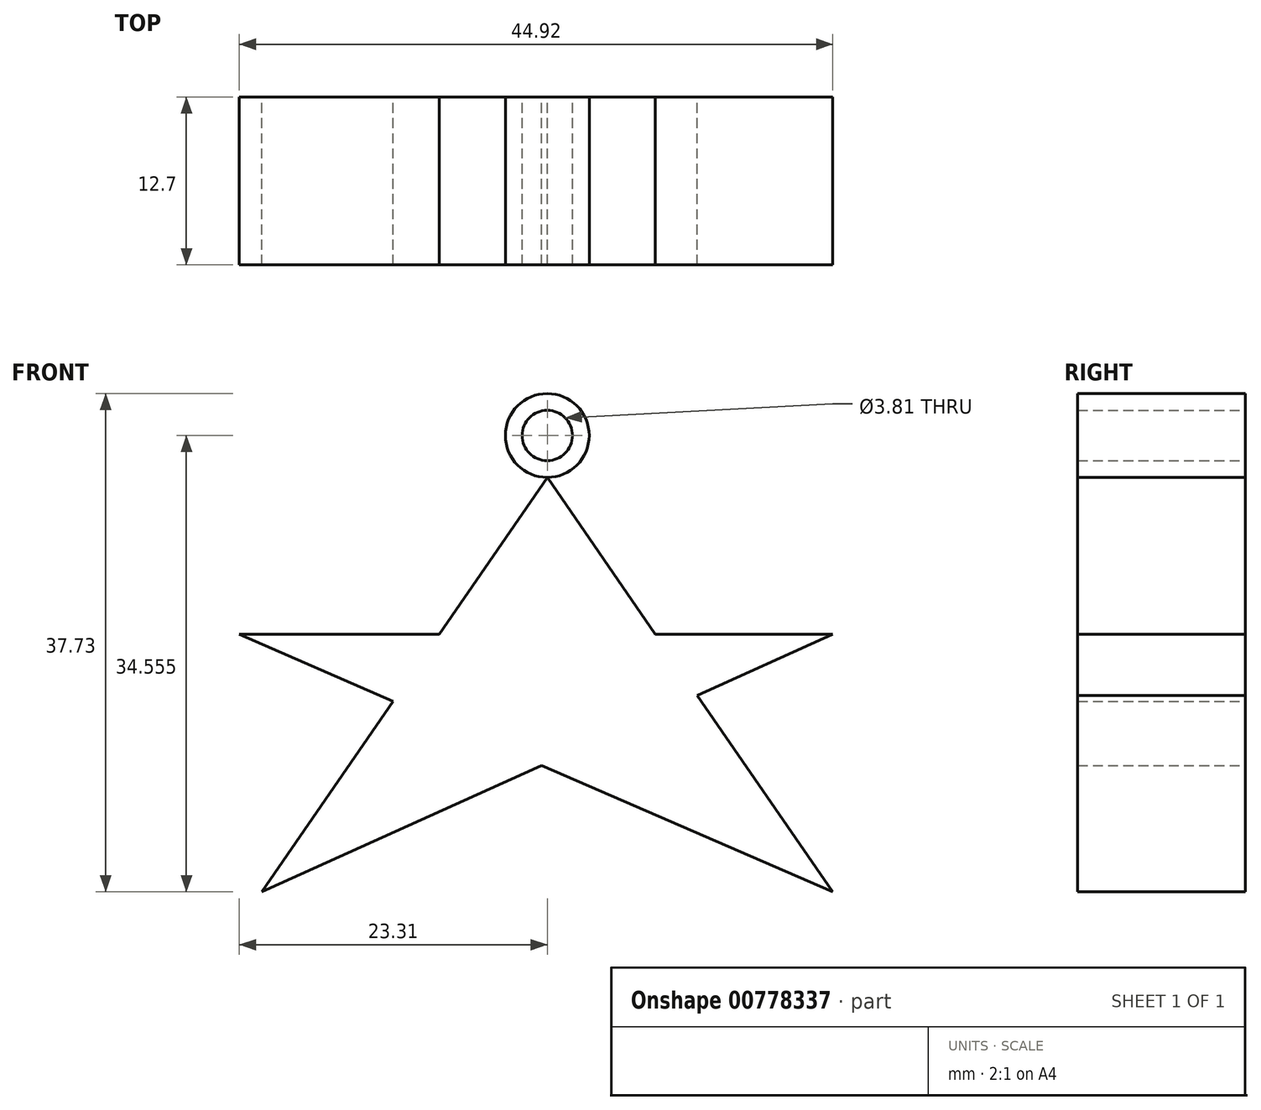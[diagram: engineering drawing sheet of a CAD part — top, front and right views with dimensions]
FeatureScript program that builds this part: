
annotation { "Feature Type Name" : "Feature", "Feature Type Description" : "" }
export const myFeature = defineFeature(function(context is Context, id is Id, definition is map)
    precondition{}
    {
        {
            var Q0;
            Q0=qCreatedBy(makeId("Front.planeOp"),FACE);
            var sketch = newSketch(context, id + "F0", { "sketchPlane" : qUnion([Q0])});
            skLineSegment(sketch, "E0", {"start": v(0, 0) * mm, "end": v(-21.6, -31.38) * mm});
            skLineSegment(sketch, "E1", {"start": v(0, 0) * mm, "end": v(21.6, -31.38) * mm});
            skLineSegment(sketch, "E2", {"start": v(21.6, -31.38) * mm, "end": v(-23.31, -11.88) * mm});
            skLineSegment(sketch, "E3", {"start": v(-23.31, -11.88) * mm, "end": v(21.6, -11.88) * mm});
            skLineSegment(sketch, "E4", {"start": v(-21.6, -31.38) * mm, "end": v(21.6, -11.88) * mm});
            skCircle(sketch, "E5", {"center": v(0, 3.18) * mm, "radius": 3.18 * mm});
            skCircle(sketch, "E6", {"center": v(0, 3.18) * mm, "radius": 1.9 * mm});
            skSolve(sketch);
        }
        {
            var Q0;
            {var subQ0=sQuery(id+"F0.wireOp",EDGE,"E3");var subQ1=sQuery(id+"F0.wireOp",EDGE,"E0");var subQ2=makeQuery(id+"F0.imprint","INTERSECT",VERTEX,{"derivedFrom":[subQ1,subQ0]});Q0=makeQuery(id+"F0.imprint","IMPRINT",FACE,{"disambiguationData":[TD([[makeQuery(id+"F0.imprint","IMPRINT",EDGE,{"disambiguationData":[TD([[subQ2,-1.0]])],"derivedFrom":subQ1}),1.0]])]});}
            var Q1;
            {var subQ1=sQuery(id+"F0.wireOp",EDGE,"E0");var subQ3=sQuery(id+"F0.wireOp",EDGE,"E3");var subQ4=makeQuery(id+"F0.imprint","INTERSECT",VERTEX,{"derivedFrom":[subQ1,subQ3]});Q1=makeQuery(id+"F0.imprint","IMPRINT",FACE,{"disambiguationData":[TD([[makeQuery(id+"F0.imprint","IMPRINT",EDGE,{"disambiguationData":[TD([[subQ4,-1.0]])],"derivedFrom":subQ3}),1.0]])]});}
            var Q2;
            Q2=makeQuery(id+"F0.imprint","IMPRINT",FACE,{"disambiguationData":[TD([[makeQuery(id+"F0.imprint","IMPRINT",EDGE,{"derivedFrom":sQuery(id+"F0.wireOp",EDGE,"E5")}),1.0]])]});
            var Q3;
            {var subQ0=sQuery(id+"F0.wireOp",EDGE,"E3");var subQ1=sQuery(id+"F0.wireOp",EDGE,"E1");var subQ2=makeQuery(id+"F0.imprint","INTERSECT",VERTEX,{"derivedFrom":[subQ1,subQ0]});Q3=makeQuery(id+"F0.imprint","IMPRINT",FACE,{"disambiguationData":[TD([[makeQuery(id+"F0.imprint","IMPRINT",EDGE,{"disambiguationData":[TD([[subQ2,-1.0]])],"derivedFrom":subQ1}),1.0]])]});}
            var Q4;
            {var subQ0=sQuery(id+"F0.wireOp",EDGE,"E2");var subQ1=sQuery(id+"F0.wireOp",EDGE,"E1");var subQ2=makeQuery(id+"F0.imprint","INTERSECT",VERTEX,{"derivedFrom":[subQ1,subQ0]});Q4=makeQuery(id+"F0.imprint","IMPRINT",FACE,{"disambiguationData":[TD([[makeQuery(id+"F0.imprint","IMPRINT",EDGE,{"disambiguationData":[TD([[subQ2,1.0]])],"derivedFrom":subQ1}),-1.0]])]});}
            var Q5;
            {var subQ0=sQuery(id+"F0.wireOp",EDGE,"E4");var subQ1=sQuery(id+"F0.wireOp",EDGE,"E0");var subQ2=makeQuery(id+"F0.imprint","INTERSECT",VERTEX,{"derivedFrom":[subQ1,subQ0]});Q5=makeQuery(id+"F0.imprint","IMPRINT",FACE,{"disambiguationData":[TD([[makeQuery(id+"F0.imprint","IMPRINT",EDGE,{"disambiguationData":[TD([[subQ2,1.0]])],"derivedFrom":subQ1}),1.0]])]});}
            var Q6;
            {var subQ0=sQuery(id+"F0.wireOp",EDGE,"E3");var subQ1=sQuery(id+"F0.wireOp",EDGE,"E0");var subQ2=makeQuery(id+"F0.imprint","INTERSECT",VERTEX,{"derivedFrom":[subQ1,subQ0]});Q6=makeQuery(id+"F0.imprint","IMPRINT",FACE,{"disambiguationData":[TD([[makeQuery(id+"F0.imprint","IMPRINT",EDGE,{"disambiguationData":[TD([[subQ2,-1.0]])],"derivedFrom":subQ1}),-1.0]])]});}
            extrude(context, id + "F1", {"entities" : qUnion([Q0, Q1, Q2, Q3, Q4, Q5, Q6]), "depth" : 12.7 * mm, "offsetDistance" : 25.4 * mm});
        }
    });
